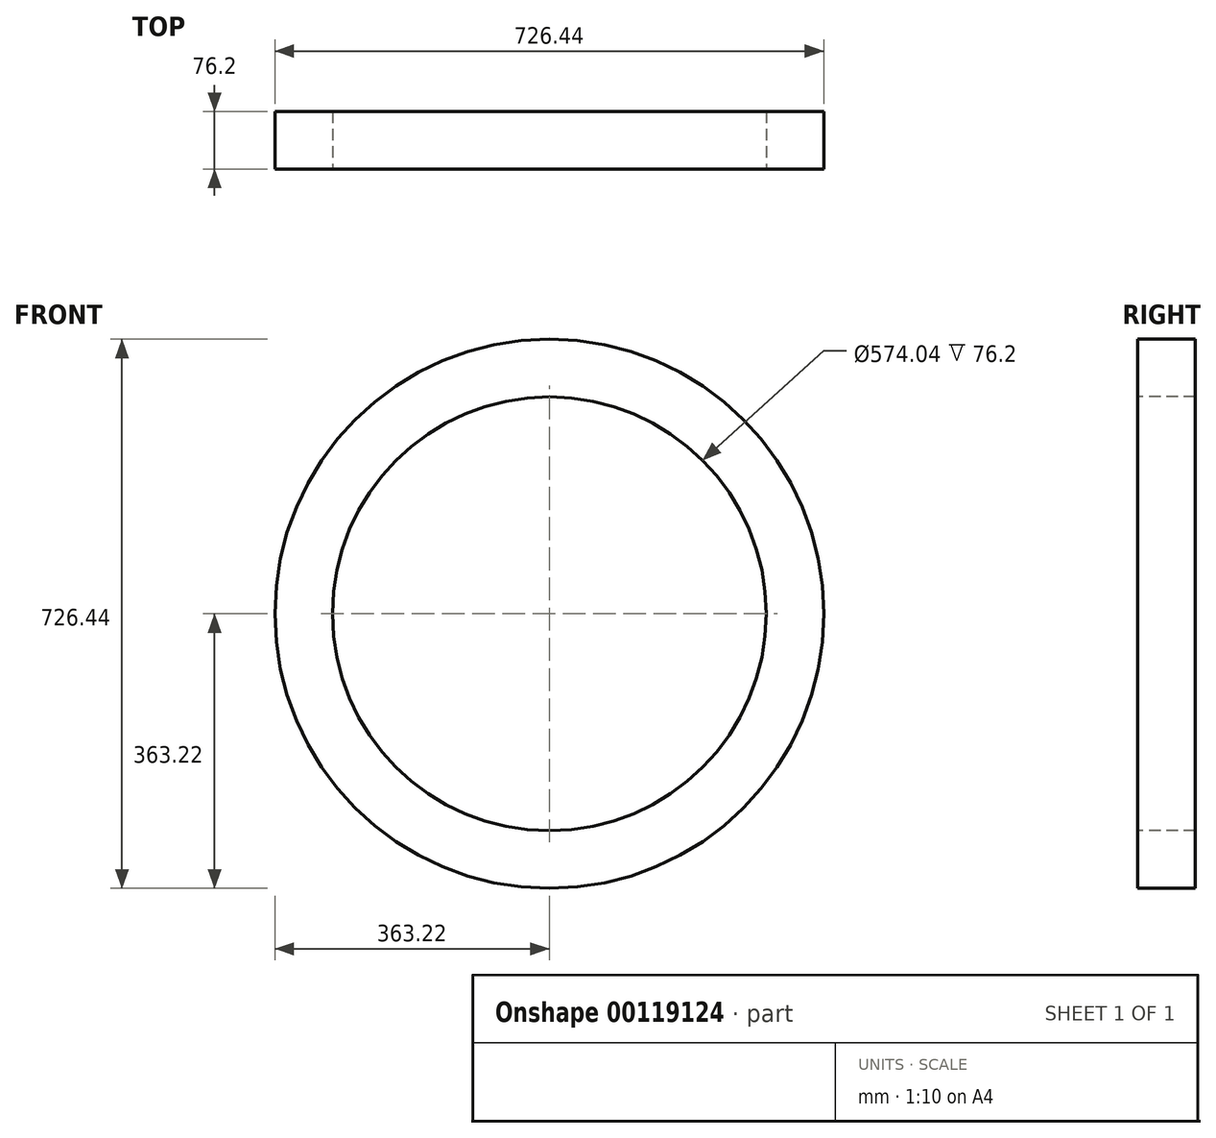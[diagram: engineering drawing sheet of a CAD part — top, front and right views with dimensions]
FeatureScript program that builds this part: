
annotation { "Feature Type Name" : "Feature", "Feature Type Description" : "" }
export const myFeature = defineFeature(function(context is Context, id is Id, definition is map)
    precondition{}
    {
        {
            var Q0;
            Q0=qCreatedBy(makeId("Top.planeOp"),FACE);
            var sketch = newSketch(context, id + "F0", { "sketchPlane" : qUnion([Q0])});
            skLineSegment(sketch, "E0", {"start": v(0, 0) * mm, "end": v(-325.12, 0) * mm, "construction": true});
            skLineSegment(sketch, "E1", {"start": v(0, 0) * mm, "end": v(0, 57.58) * mm, "construction": true});
            skLineSegment(sketch, "E2.bottom", {"start": v(-287.02, 38.1) * mm, "end": v(-363.22, 38.1) * mm});
            skLineSegment(sketch, "E2.top", {"start": v(-287.02, -38.1) * mm, "end": v(-363.22, -38.1) * mm});
            skLineSegment(sketch, "E2.left", {"start": v(-287.02, 38.1) * mm, "end": v(-287.02, -38.1) * mm});
            skLineSegment(sketch, "E2.right", {"start": v(-363.22, 38.1) * mm, "end": v(-363.22, -38.1) * mm});
            skPoint(sketch, "E2.middle", {"position": v(-325.12, 0) * mm});
            skSolve(sketch);
        }
        {
            var Q0;
            Q0=makeQuery(id+"F0.imprint","IMPRINT",FACE,{"disambiguationData":[TD([[makeQuery(id+"F0.imprint","IMPRINT",EDGE,{"derivedFrom":sQuery(id+"F0.wireOp",EDGE,"E2.bottom")}),1.0]])]});
            var Q1;
            Q1=sQuery(id+"F0.wireOp",EDGE,"E1");
            revolve(context, id + "F1", {"entities" : qUnion([Q0]), "axis" : qUnion([Q1]), "revolveType" : RevolveType.FULL});
        }
    });
